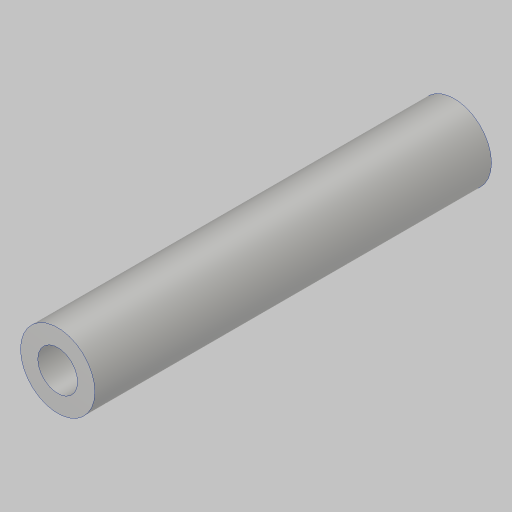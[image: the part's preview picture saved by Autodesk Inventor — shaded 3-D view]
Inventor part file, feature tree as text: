
AUTODESK INVENTOR PART (.ipt)
format: ipt  version: 2023.5 (Build 275446000, 446)  size: 103,936 bytes
history: native  units: in
note: dims shown in document units (in); Inventor stores cm internally (conversion verified against a paired STEP export)
features: extrude x1, hole x1
ambient origin geometry x8: Origin, YZ Plane, XZ Plane, XY Plane, X Axis, Y Axis, Z Axis, Center Point
bodies: Solid1 (feature_tree)
feature tree (2):
  extrude  "Extrusion1"  Depth=2.0in
  hole  "Hole1"  [1 undecoded]
note: 1 required parameter value undecoded (feature->parameter linkage not recoverable at this tier; creation-order binding heuristic only, values carry confidence <= 0.55)
